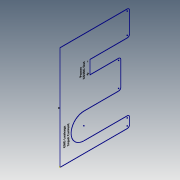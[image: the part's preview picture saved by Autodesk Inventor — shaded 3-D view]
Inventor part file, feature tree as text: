
AUTODESK INVENTOR PART (.ipt)
format: ipt  version: 2020.5 (Build 245400000, 400)  size: 133,632 bytes
history: native  units: mm
features: sketch x1
ambient origin geometry x8: Origin, YZ Plane, XZ Plane, XY Plane, X Axis, Y Axis, Z Axis, Center Point
feature tree (1):
  sketch  "Sketch31"  dims[d13=18.0mm d14=60.0mm d684=2.7mm d685=19.1mm d686=2.7mm d687=18.6mm d688=36.361013mm d689=4.351086mm d690=36.611013mm d691=8.051086mm d692=2.1mm d693=8.9mm d694=2.1mm d695=15.2mm d696=0.599999mm d697=1.799998mm d698=2.599986mm d699=3.299982mm d700=26.905472mm d701=12.841302mm d702=23.305472mm d703=11.859893mm d704=20.205472mm d705=15.009893mm d706=27.89455mm d707=24.218985mm]
